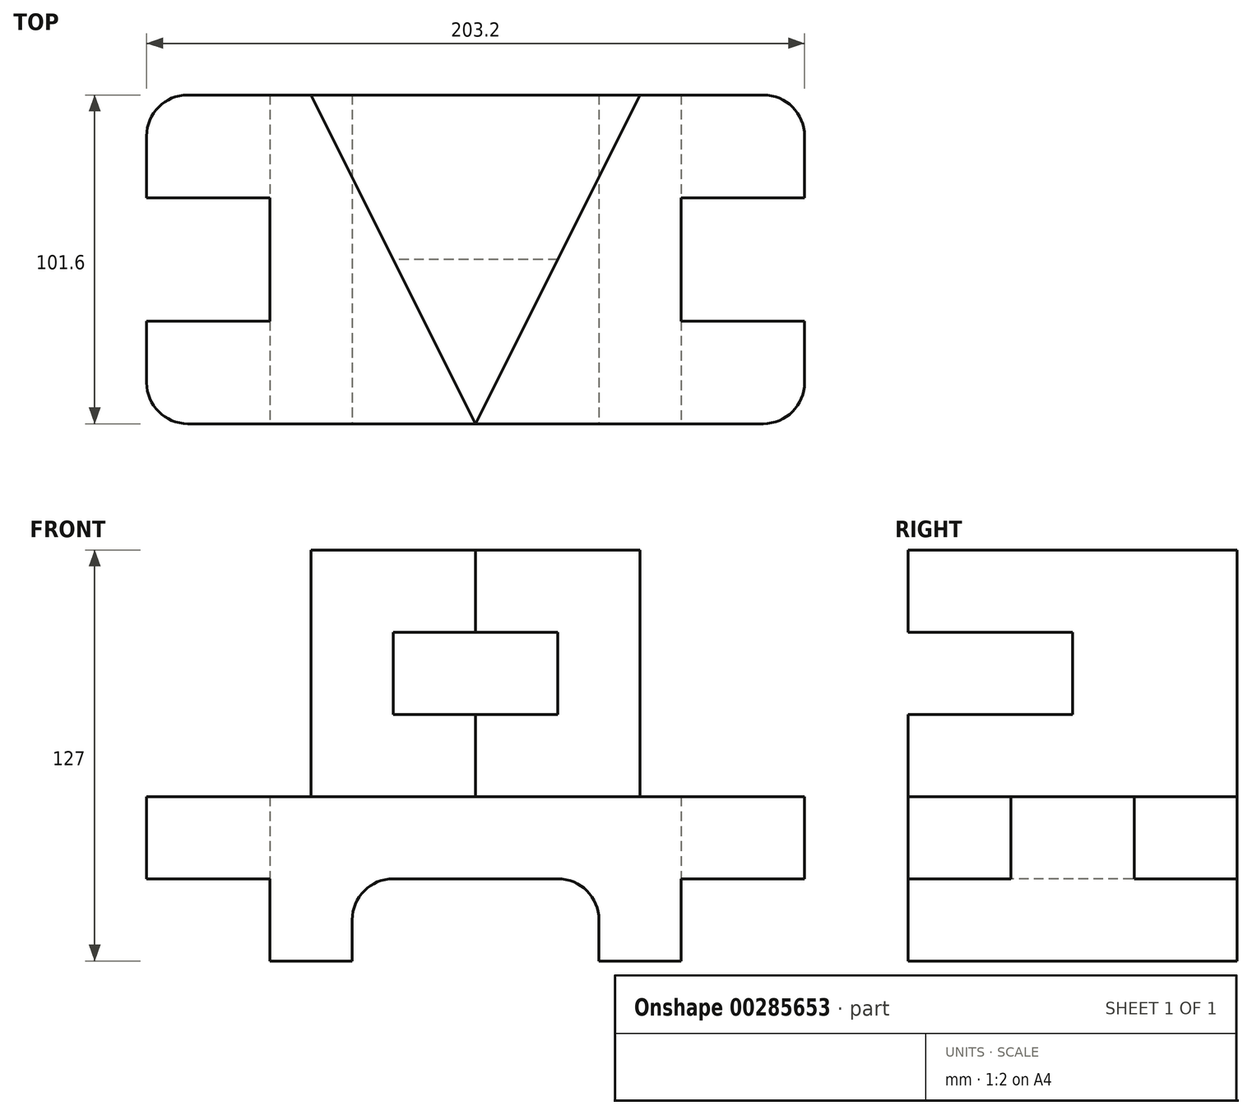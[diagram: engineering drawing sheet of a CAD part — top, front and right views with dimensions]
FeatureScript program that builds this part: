
annotation { "Feature Type Name" : "Feature", "Feature Type Description" : "" }
export const myFeature = defineFeature(function(context is Context, id is Id, definition is map)
    precondition{}
    {
        {
            var Q0;
            Q0=qCreatedBy(makeId("Top.planeOp"),FACE);
            var sketch = newSketch(context, id + "F0", { "sketchPlane" : qUnion([Q0])});
            skLineSegment(sketch, "E0", {"start": v(0, 0) * mm, "end": v(203.2, 0) * mm});
            skLineSegment(sketch, "E1", {"start": v(203.2, 0) * mm, "end": v(203.2, 31.75) * mm});
            skLineSegment(sketch, "E2", {"start": v(203.2, 31.75) * mm, "end": v(165.1, 31.75) * mm});
            skLineSegment(sketch, "E3", {"start": v(165.1, 31.75) * mm, "end": v(165.1, 69.85) * mm});
            skLineSegment(sketch, "E4", {"start": v(165.1, 69.85) * mm, "end": v(203.2, 69.85) * mm});
            skLineSegment(sketch, "E5", {"start": v(203.2, 69.85) * mm, "end": v(203.2, 101.6) * mm});
            skLineSegment(sketch, "E6", {"start": v(203.2, 101.6) * mm, "end": v(0, 101.6) * mm});
            skLineSegment(sketch, "E7", {"start": v(0, 101.6) * mm, "end": v(0, 69.85) * mm});
            skLineSegment(sketch, "E8", {"start": v(0, 69.85) * mm, "end": v(38.1, 69.85) * mm});
            skLineSegment(sketch, "E9", {"start": v(38.1, 69.85) * mm, "end": v(38.1, 31.75) * mm});
            skLineSegment(sketch, "E10", {"start": v(38.1, 31.75) * mm, "end": v(0, 31.75) * mm});
            skLineSegment(sketch, "E11", {"start": v(0, 31.75) * mm, "end": v(0, 0) * mm});
            skLineSegment(sketch, "E12", {"start": v(101.6, 0) * mm, "end": v(101.6, 101.6) * mm, "construction": true});
            skSolve(sketch);
        }
        {
            var Q0;
            Q0 = qSketchRegion(id + "F0", true);
            extrude(context, id + "F1", {"entities" : qUnion([Q0]), "depth" : 25.4 * mm});
        }
        {
            var Q0;
            Q0=makeQuery(id+"F1.opExtrude","SWEPT_EDGE",EDGE,{"disambiguationData":[OSD([sQuery(id+"F0.wireOp",EDGE,"E0"),sQuery(id+"F0.wireOp",EDGE,"E1")])]});
            var Q1;
            Q1=makeQuery(id+"F1.opExtrude","SWEPT_EDGE",EDGE,{"disambiguationData":[OSD([sQuery(id+"F0.wireOp",EDGE,"E5"),sQuery(id+"F0.wireOp",EDGE,"E6")])]});
            var Q2;
            Q2=makeQuery(id+"F1.opExtrude","SWEPT_EDGE",EDGE,{"disambiguationData":[OSD([sQuery(id+"F0.wireOp",EDGE,"E0"),sQuery(id+"F0.wireOp",EDGE,"E11")])]});
            var Q3;
            Q3=makeQuery(id+"F1.opExtrude","SWEPT_EDGE",EDGE,{"disambiguationData":[OSD([sQuery(id+"F0.wireOp",EDGE,"E6"),sQuery(id+"F0.wireOp",EDGE,"E7")])]});
            fillet(context, id + "F2", {"entities" : qUnion([Q0, Q1, Q2, Q3]), "radius" : 12.7 * mm, "tangentPropagation" : true, "allowEdgeOverflow" : false});
        }
        {
            var Q0;
            Q0=qCreatedBy(makeId("Front.planeOp"),FACE);
            var sketch = newSketch(context, id + "F3", { "sketchPlane" : qUnion([Q0])});
            skLineSegment(sketch, "E13", {"start": v(38.1, 0) * mm, "end": v(38.1, -25.4) * mm});
            skLineSegment(sketch, "E14", {"start": v(38.1, -25.4) * mm, "end": v(63.5, -25.4) * mm});
            skLineSegment(sketch, "E15", {"start": v(139.7, -25.4) * mm, "end": v(165.1, -25.4) * mm});
            skLineSegment(sketch, "E16", {"start": v(165.1, -25.4) * mm, "end": v(165.1, 0) * mm});
            skLineSegment(sketch, "E17", {"start": v(63.5, -25.4) * mm, "end": v(63.5, -12.7) * mm});
            skArc(sketch, "E18", {"start": v(76.2, 0) * mm, "mid": v(67.22, -3.72) * mm, "end": v(63.5, -12.7) * mm});
            skArc(sketch, "E19", {"start": v(139.7, -12.7) * mm, "mid": v(135.98, -3.72) * mm, "end": v(127, 0) * mm});
            skLineSegment(sketch, "E20", {"start": v(139.7, -12.7) * mm, "end": v(139.7, -25.4) * mm});
            skLineSegment(sketch, "E21", {"start": v(38.1, 0) * mm, "end": v(76.2, 0) * mm});
            skLineSegment(sketch, "E22", {"start": v(127, 0) * mm, "end": v(165.1, 0) * mm});
            skSolve(sketch);
        }
        {
            var Q0;
            Q0 = qSketchRegion(id + "F3", true);
            extrude(context, id + "F4", {"entities" : qUnion([Q0]), "operationType" : NewBodyOperationType.ADD, "oppositeDirection" : true, "depth" : 101.6 * mm});
        }
        {
            var Q0;
            Q0=makeQuery(id+"F1.opExtrude","CAP_FACE",FACE,{"disambiguationData":[OSD([sQuery(id+"F0.wireOp",EDGE,"E0"),sQuery(id+"F0.wireOp",EDGE,"E1"),sQuery(id+"F0.wireOp",EDGE,"E2"),sQuery(id+"F0.wireOp",EDGE,"E3"),sQuery(id+"F0.wireOp",EDGE,"E4"),sQuery(id+"F0.wireOp",EDGE,"E5"),sQuery(id+"F0.wireOp",EDGE,"E6"),sQuery(id+"F0.wireOp",EDGE,"E7"),sQuery(id+"F0.wireOp",EDGE,"E8"),sQuery(id+"F0.wireOp",EDGE,"E9"),sQuery(id+"F0.wireOp",EDGE,"E10"),sQuery(id+"F0.wireOp",EDGE,"E11")])],"isStart":false});
            var sketch = newSketch(context, id + "F5", { "sketchPlane" : qUnion([Q0])});
            skLineSegment(sketch, "E23", {"start": v(152.4, 101.6) * mm, "end": v(101.6, 0) * mm});
            skLineSegment(sketch, "E24", {"start": v(101.6, 0) * mm, "end": v(50.8, 101.6) * mm});
            skLineSegment(sketch, "E25", {"start": v(50.8, 101.6) * mm, "end": v(152.4, 101.6) * mm});
            skLineSegment(sketch, "E26", {"start": v(101.6, 101.6) * mm, "end": v(101.6, 0) * mm, "construction": true});
            skSolve(sketch);
        }
        {
            var Q0;
            Q0 = qSketchRegion(id + "F5", true);
            extrude(context, id + "F6", {"entities" : qUnion([Q0]), "operationType" : NewBodyOperationType.ADD, "depth" : 76.2 * mm});
        }
        {
            var Q0;
            Q0=qCreatedBy(makeId("Right.planeOp"),FACE);
            var sketch = newSketch(context, id + "F7", { "sketchPlane" : qUnion([Q0])});
            skLineSegment(sketch, "E27", {"start": v(0, 50.8) * mm, "end": v(50.8, 50.8) * mm});
            skLineSegment(sketch, "E28", {"start": v(50.8, 50.8) * mm, "end": v(50.8, 76.2) * mm});
            skLineSegment(sketch, "E29", {"start": v(50.8, 76.2) * mm, "end": v(0, 76.2) * mm});
            skLineSegment(sketch, "E30", {"start": v(0, 76.2) * mm, "end": v(0, 50.8) * mm});
            skSolve(sketch);
        }
        {
            var Q0;
            Q0 = qSketchRegion(id + "F7", true);
            extrude(context, id + "F8", {"entities" : qUnion([Q0]), "operationType" : NewBodyOperationType.REMOVE, "endBound" : BoundingType.THROUGH_ALL, "depth" : 25.4 * mm});
        }
    });
